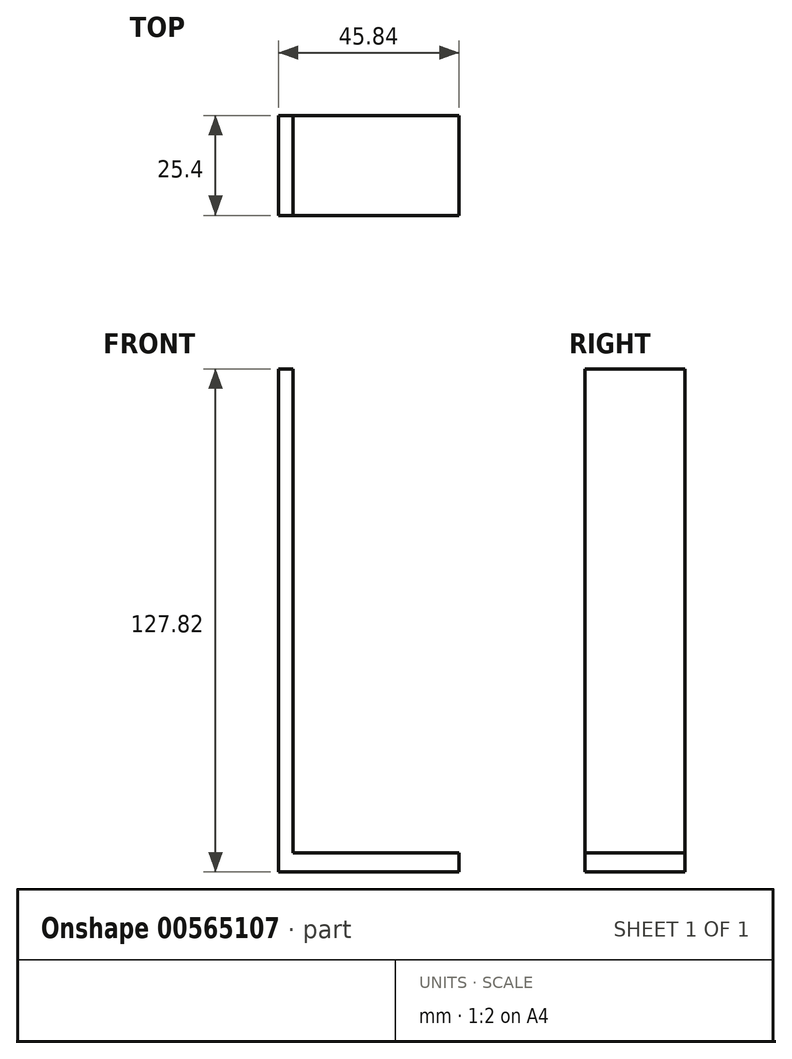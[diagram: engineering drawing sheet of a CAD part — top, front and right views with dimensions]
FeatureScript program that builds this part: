
annotation { "Feature Type Name" : "Feature", "Feature Type Description" : "" }
export const myFeature = defineFeature(function(context is Context, id is Id, definition is map)
    precondition{}
    {
        {
            var Q0;
            Q0=qCreatedBy(makeId("Top.planeOp"),FACE);
            var sketch = newSketch(context, id + "F0", { "sketchPlane" : qUnion([Q0])});
            skCircle(sketch, "E0", {"center": v(0, 0) * mm, "radius": 56.21 * mm});
            skSolve(sketch);
        }
        {
            var Q0;
            Q0=sQuery(id+"F0.wireOp",EDGE,"E0");
            extrude(context, id + "F1", {"bodyType" : ToolBodyType.SURFACE, "surfaceEntities" : qUnion([Q0]), "depth" : 63.28 * mm, "offsetDistance" : 25.4 * mm});
        }
        {
            var Q0;
            Q0=qCreatedBy(makeId("Front.planeOp"),FACE);
            var sketch = newSketch(context, id + "F2", { "sketchPlane" : qUnion([Q0])});
            skLineSegment(sketch, "E1.bottom", {"start": v(55.52, 63.1) * mm, "end": v(59.22, 63.1) * mm});
            skLineSegment(sketch, "E1.left", {"start": v(55.52, 63.1) * mm, "end": v(55.52, -59.87) * mm});
            skLineSegment(sketch, "E1.right", {"start": v(59.22, 63.1) * mm, "end": v(59.22, -59.87) * mm});
            skLineSegment(sketch, "E2.bottom", {"start": v(59.22, -59.87) * mm, "end": v(101.36, -59.87) * mm});
            skLineSegment(sketch, "E2.top", {"start": v(55.52, -64.7) * mm, "end": v(101.36, -64.7) * mm});
            skLineSegment(sketch, "E2.left", {"start": v(55.52, -59.87) * mm, "end": v(55.52, -64.7) * mm});
            skLineSegment(sketch, "E2.right", {"start": v(101.36, -59.87) * mm, "end": v(101.36, -64.7) * mm});
            skSolve(sketch);
        }
        {
            var Q0;
            Q0 = qSketchRegion(id + "F2", true);
            extrude(context, id + "F3", {"entities" : qUnion([Q0]), "endBound" : BoundingType.SYMMETRIC, "depth" : 25.4 * mm, "offsetDistance" : 25.4 * mm});
        }
    });
